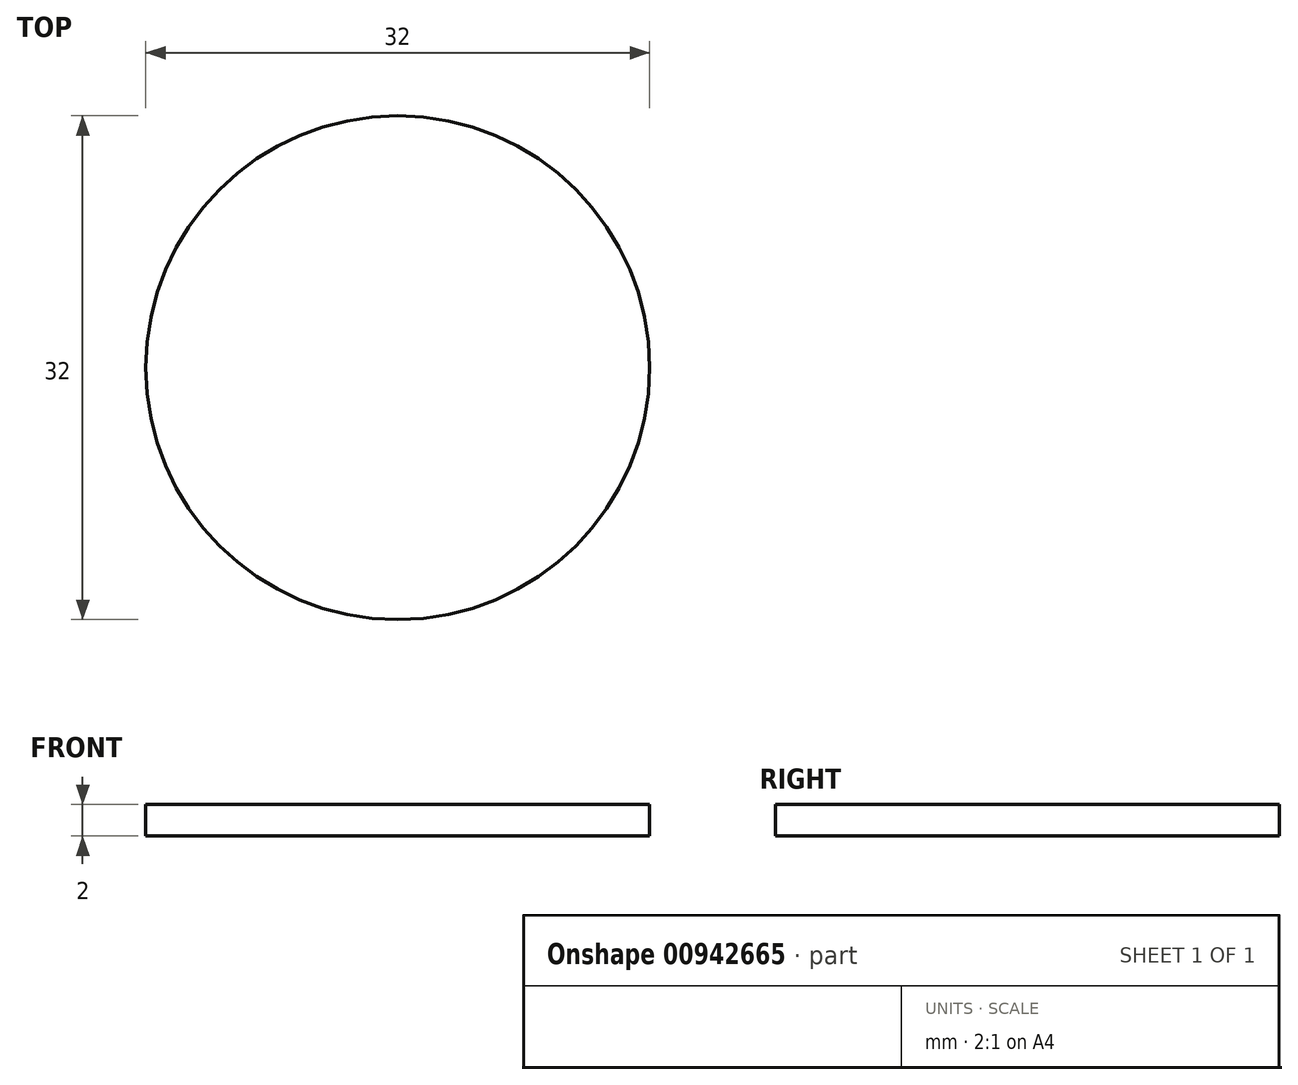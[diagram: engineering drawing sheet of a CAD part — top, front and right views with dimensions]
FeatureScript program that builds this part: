
annotation { "Feature Type Name" : "Feature", "Feature Type Description" : "" }
export const myFeature = defineFeature(function(context is Context, id is Id, definition is map)
    precondition{}
    {
        {
            var Q0;
            Q0=qCreatedBy(makeId("Top.planeOp"),FACE);
            var sketch = newSketch(context, id + "F0", { "sketchPlane" : qUnion([Q0])});
            skCircle(sketch, "E0", {"center": v(0, 0) * mm, "radius": 16 * mm});
            skSolve(sketch);
        }
        {
            var Q0;
            Q0=makeQuery(id+"F0.imprint","IMPRINT",FACE,{"disambiguationData":[TD([[makeQuery(id+"F0.imprint","IMPRINT",EDGE,{"derivedFrom":sQuery(id+"F0.wireOp",EDGE,"E0")}),1.0]])]});
            extrude(context, id + "F1", {"entities" : qUnion([Q0]), "depth" : 2 * mm, "offsetDistance" : 25 * mm});
        }
    });
